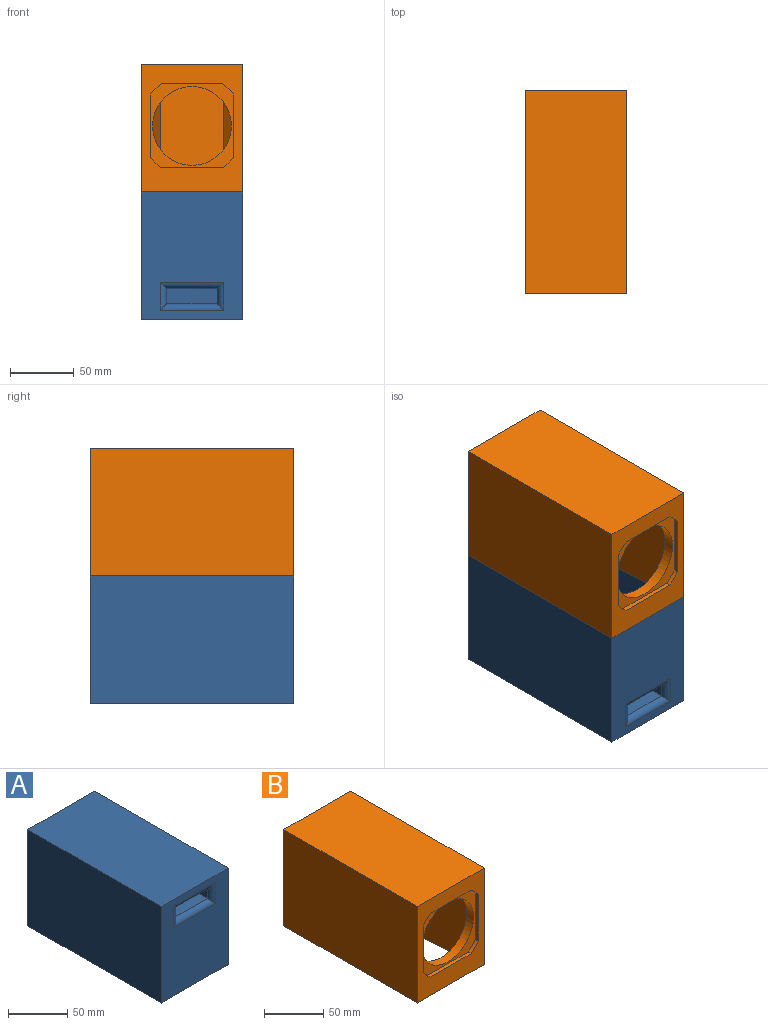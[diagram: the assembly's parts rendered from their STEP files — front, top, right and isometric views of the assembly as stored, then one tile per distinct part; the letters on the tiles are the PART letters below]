
ASSEMBLY  parts=2 mates=1
PART A: 23 faces, bbox 80x160x100 mm
  f0: plane 100x80mm, normal (0,-1,0), area 6900mm2, adj f4,f5,f7,f8,f19,f20,f21,f22
  f1: plane 52x25mm, normal (0,1,0), area 820mm2, adj f3,f12,f13,f14,f15,f16,f17,f18
  f2: plane 94x68mm, normal (0,1,0), area 5092mm2, adj f3,f8,f9,f11,f12,f13,f14
  f3: plane 142x68mm, normal (0,0,-1), area 3282mm2, adj f1,f2,f9,f10,f11,f12,f13
  f4: plane 160x100mm, normal (-1,0,0), area 16000mm2, adj f0,f6,f7,f8
  f5: plane 160x100mm, normal (1,0,0), area 16000mm2, adj f0,f6,f7,f8
  f6: plane 100x80mm, normal (0,1,0), area 8000mm2, adj f4,f5,f7,f8
  f7: plane 160x80mm, normal (0,0,1), area 12800mm2, adj f0,f4,f5,f6
  f8: plane 160x80mm, normal (0,0,-1), area 4422mm2, adj f0,f2,f4,f5,f6,f9,f10,f11
  f9: plane 142x94mm, normal (1,-0.06,0), area 13374.8mm2, adj f2,f3,f8,f10
  f10: plane 94x50mm, normal (0,-1,0), area 4700mm2, adj f3,f8,f9,f11
  f11: plane 142x94mm, normal (-1,-0.06,0), area 13374.8mm2, adj f2,f3,f8,f10
  f12: plane 98x25mm, normal (-1,0,0), area 2450mm2, adj f1,f2,f3,f14
  f13: plane 98x25mm, normal (1,0,0), area 2450mm2, adj f1,f2,f3,f14
  f14: plane 98x52mm, normal (0,0,-1), area 5096mm2, adj f1,f2,f12,f13
  f15: plane 105x12mm, normal (-1,0,0), area 1260mm2, adj f1,f16,f17,f20
  f16: plane 105x40mm, normal (0,0,1), area 4200mm2, adj f1,f15,f18,f19
  f17: plane 105x40mm, normal (0,0,-1), area 4200mm2, adj f1,f15,f18,f22
  f18: plane 105x12mm, normal (1,0,0), area 1260mm2, adj f1,f16,f17,f21
  f19: cylinder r=5mm len=50mm, axis (1,0,0), area 342.7mm2, adj f0,f16,f20,f21
  f20: cylinder r=5mm len=22mm, axis (0,0,1), area 122.8mm2, adj f0,f15,f19,f22
  f21: cylinder r=5mm len=22mm, axis (0,0,-1), area 122.8mm2, adj f0,f18,f19,f22
  f22: cylinder r=5mm len=50mm, axis (-1,0,0), area 342.7mm2, adj f0,f17,f20,f21
PART B: 21 faces, bbox 80x160x100 mm
  f0: plane 100x80mm, normal (0,-1,0), area 3779.2mm2, adj f1,f2,f4,f5,f11,f12,f13,f14
  f1: plane 160x100mm, normal (-1,0,0), area 16000mm2, adj f0,f3,f4,f5
  f2: plane 160x100mm, normal (1,0,0), area 16000mm2, adj f0,f3,f4,f5
  f3: plane 100x80mm, normal (0,1,0), area 8000mm2, adj f1,f2,f4,f5
  f4: plane 160x80mm, normal (0,0,1), area 12800mm2, adj f0,f1,f2,f3
  f5: plane 160x80mm, normal (0,0,-1), area 4422mm2, adj f0,f1,f2,f3,f6,f7,f8,f9
  f6: plane 142x94mm, normal (1,-0.06,0), area 13374.8mm2, adj f5,f7,f9,f10
  f7: plane 94x50mm, normal (0,-1,0), area 4700mm2, adj f5,f6,f8,f10
  f8: plane 142x94mm, normal (-1,-0.06,0), area 13374.8mm2, adj f5,f7,f9,f10
  f9: plane 94x68mm, normal (0,1,0), area 3372.9mm2, adj f5,f6,f8,f10,f20
  f10: plane 142x68mm, normal (0,0,-1), area 8378mm2, adj f6,f7,f8,f9
  f11: cylinder r=41mm len=8.67mm, axis (0,-1,0), area 43.1mm2, adj f0,f12,f18,f19
  f12: plane 48.66x3.5mm, normal (-1,0,0), area 170.3mm2, adj f0,f11,f13,f19
  f13: cylinder r=41mm len=8.67mm, axis (0,-1,0), area 43.1mm2, adj f0,f12,f14,f19
  f14: plane 48.66x3.5mm, normal (0,0,-1), area 170.3mm2, adj f0,f13,f15,f19
  f15: cylinder r=41mm len=8.67mm, axis (0,-1,0), area 43.1mm2, adj f0,f14,f16,f19
  f16: plane 48.66x3.5mm, normal (1,0,0), area 170.3mm2, adj f0,f15,f17,f19
  f17: cylinder r=41mm len=8.67mm, axis (0,-1,0), area 43.1mm2, adj f0,f16,f18,f19
  f18: plane 48.66x3.5mm, normal (0,0,1), area 170.3mm2, adj f0,f11,f17,f19
  f19: plane 66x66mm, normal (0,-1,0), area 1201.7mm2, adj f11,f12,f13,f14,f15,f16,f17,f18
  f20: cylinder r=31mm len=62mm, axis (0,-1,0), area 1655.6mm2, adj f9,f19
PLACE A rot(axis=(0,1,0),180deg) t=(3.26,27.78,11.35)mm
PLACE B t=(3.26,27.78,11.35)mm
MATE planar A.f8 <-> B.f5  axis (0,0,-1) through (-36.74,-37.22,11.35)mm
